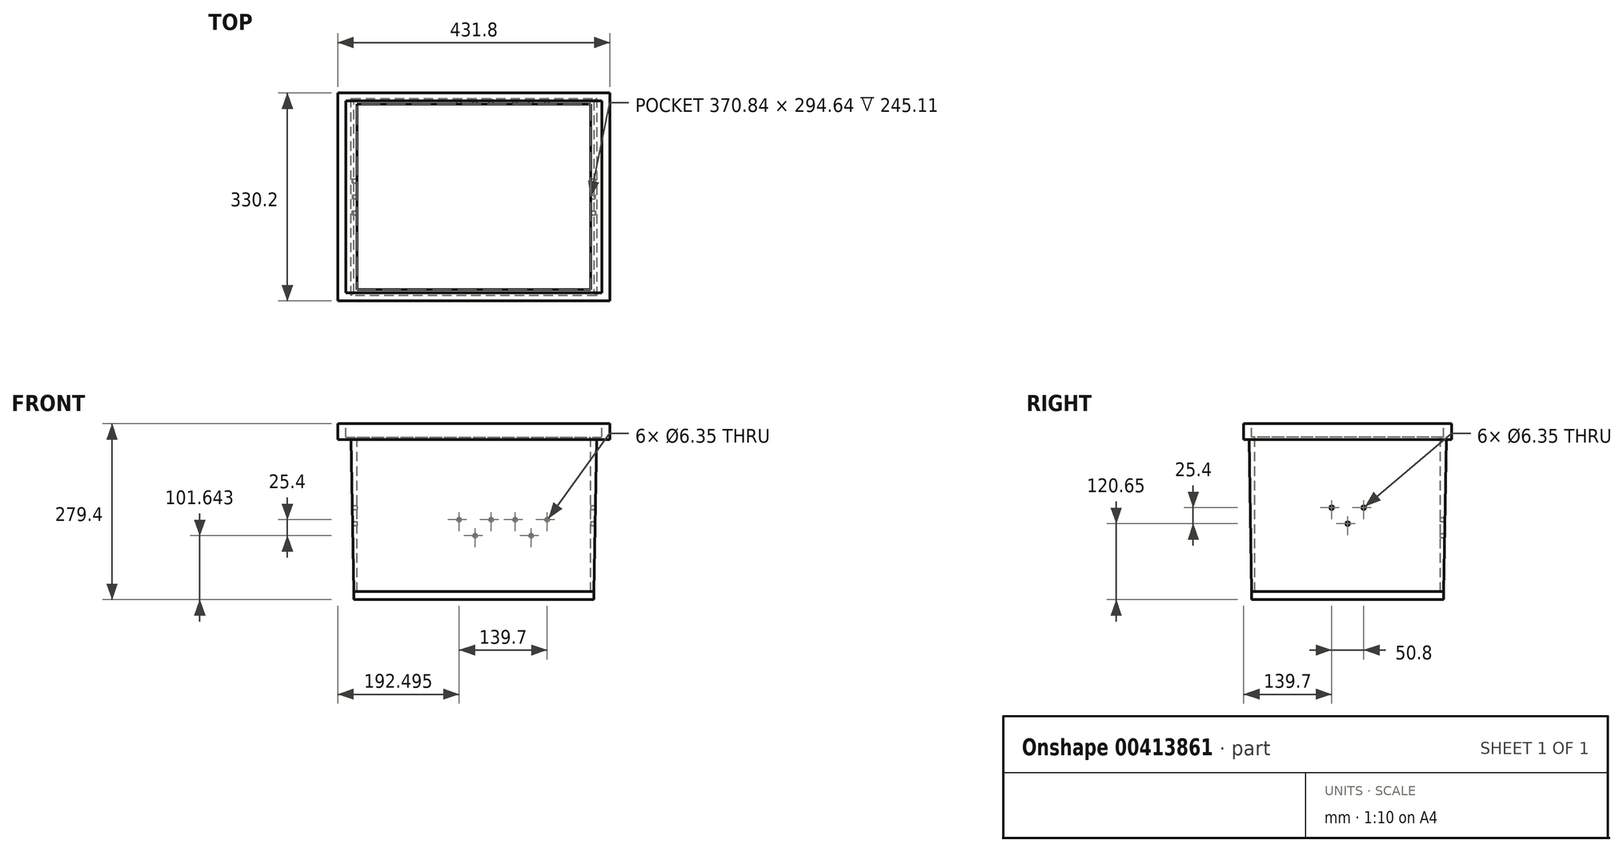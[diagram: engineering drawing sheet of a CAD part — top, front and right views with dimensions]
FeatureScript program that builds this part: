
annotation { "Feature Type Name" : "Feature", "Feature Type Description" : "" }
export const myFeature = defineFeature(function(context is Context, id is Id, definition is map)
    precondition{}
    {
        {
            var Q0;
            Q0=qCreatedBy(makeId("Top.planeOp"),FACE);
            var sketch = newSketch(context, id + "F0", { "sketchPlane" : qUnion([Q0])});
            skLineSegment(sketch, "E0.bottom", {"start": v(-190.5, 152.4) * mm, "end": v(190.5, 152.4) * mm});
            skLineSegment(sketch, "E0.top", {"start": v(-190.5, -152.4) * mm, "end": v(190.5, -152.4) * mm});
            skLineSegment(sketch, "E0.left", {"start": v(-190.5, 152.4) * mm, "end": v(-190.5, -152.4) * mm});
            skLineSegment(sketch, "E0.right", {"start": v(190.5, 152.4) * mm, "end": v(190.5, -152.4) * mm});
            skPoint(sketch, "E0.middle", {"position": v(0, 0) * mm});
            skLineSegment(sketch, "E1.0", {"start": v(-185.42, -147.32) * mm, "end": v(185.42, -147.32) * mm});
            skLineSegment(sketch, "E1.1", {"start": v(-185.42, 147.32) * mm, "end": v(-185.42, -147.32) * mm});
            skLineSegment(sketch, "E1.2", {"start": v(-185.42, 147.32) * mm, "end": v(185.42, 147.32) * mm});
            skLineSegment(sketch, "E1.3", {"start": v(185.42, 147.32) * mm, "end": v(185.42, -147.32) * mm});
            skSolve(sketch);
        }
        {
            var Q0;
            Q0 = qSketchRegion(id + "F0", true);
            extrude(context, id + "F1", {"entities" : qUnion([Q0]), "depth" : 241.3 * mm, "hasDraft" : true, "draftAngle" : 1 * degree});
        }
        {
            var Q0;
            Q0=makeQuery(id+"F1.opExtrude","CAP_FACE",FACE,{"disambiguationData":[OSD([sQuery(id+"F0.wireOp",EDGE,"E0.bottom"),sQuery(id+"F0.wireOp",EDGE,"E0.top"),sQuery(id+"F0.wireOp",EDGE,"E0.left"),sQuery(id+"F0.wireOp",EDGE,"E0.right"),sQuery(id+"F0.wireOp",EDGE,"E1.0"),sQuery(id+"F0.wireOp",EDGE,"E1.1"),sQuery(id+"F0.wireOp",EDGE,"E1.2"),sQuery(id+"F0.wireOp",EDGE,"E1.3")])],"isStart":false});
            var sketch = newSketch(context, id + "F2", { "sketchPlane" : qUnion([Q0])});
            skLineSegment(sketch, "E2.bottom", {"start": v(-215.9, 165.1) * mm, "end": v(215.9, 165.1) * mm});
            skLineSegment(sketch, "E2.top", {"start": v(-215.9, -165.1) * mm, "end": v(215.9, -165.1) * mm});
            skLineSegment(sketch, "E2.left", {"start": v(-215.9, 165.1) * mm, "end": v(-215.9, -165.1) * mm});
            skLineSegment(sketch, "E2.right", {"start": v(215.9, 165.1) * mm, "end": v(215.9, -165.1) * mm});
            skPoint(sketch, "E2.middle", {"position": v(0, 0) * mm});
            skSolve(sketch);
        }
        {
            var Q0;
            Q0 = qSketchRegion(id + "F2", true);
            extrude(context, id + "F3", {"entities" : qUnion([Q0]), "operationType" : NewBodyOperationType.ADD, "depth" : 25.4 * mm});
        }
        {
            var Q0;
            Q0=makeQuery(id+"F1.opExtrude","CAP_FACE",FACE,{"disambiguationData":[OSD([sQuery(id+"F0.wireOp",EDGE,"E0.bottom"),sQuery(id+"F0.wireOp",EDGE,"E0.top"),sQuery(id+"F0.wireOp",EDGE,"E0.left"),sQuery(id+"F0.wireOp",EDGE,"E0.right"),sQuery(id+"F0.wireOp",EDGE,"E1.0"),sQuery(id+"F0.wireOp",EDGE,"E1.1"),sQuery(id+"F0.wireOp",EDGE,"E1.2"),sQuery(id+"F0.wireOp",EDGE,"E1.3")])],"isStart":true});
            var sketch = newSketch(context, id + "F4", { "sketchPlane" : qUnion([Q0])});
            skLineSegment(sketch, "E3.0", {"start": v(-190.5, -152.4) * mm, "end": v(-190.5, 152.4) * mm});
            skLineSegment(sketch, "E3.1", {"start": v(-190.5, 152.4) * mm, "end": v(190.5, 152.4) * mm});
            skLineSegment(sketch, "E3.2", {"start": v(-190.5, -152.4) * mm, "end": v(190.5, -152.4) * mm});
            skLineSegment(sketch, "E3.3", {"start": v(190.5, -152.4) * mm, "end": v(190.5, 152.4) * mm});
            skSolve(sketch);
        }
        {
            var Q0;
            Q0 = qSketchRegion(id + "F4", true);
            extrude(context, id + "F5", {"entities" : qUnion([Q0]), "operationType" : NewBodyOperationType.ADD, "depth" : 12.7 * mm});
        }
        {
            var Q0;
            Q0=makeQuery(id+"F3.opExtrude","CAP_FACE",FACE,{"disambiguationData":[OSD([sQuery(id+"F2.wireOp",EDGE,"E2.bottom"),sQuery(id+"F2.wireOp",EDGE,"E2.top"),sQuery(id+"F2.wireOp",EDGE,"E2.left"),sQuery(id+"F2.wireOp",EDGE,"E2.right")])],"isStart":false});
            var sketch = newSketch(context, id + "F6", { "sketchPlane" : qUnion([Q0])});
            skLineSegment(sketch, "E4.0", {"start": v(-215.9, 165.1) * mm, "end": v(215.9, 165.1) * mm});
            skLineSegment(sketch, "E4.1", {"start": v(215.9, 165.1) * mm, "end": v(215.9, -165.1) * mm});
            skLineSegment(sketch, "E4.2", {"start": v(-215.9, -165.1) * mm, "end": v(215.9, -165.1) * mm});
            skLineSegment(sketch, "E4.3", {"start": v(-215.9, 165.1) * mm, "end": v(-215.9, -165.1) * mm});
            skLineSegment(sketch, "E5.0", {"start": v(-203.2, 152.4) * mm, "end": v(203.2, 152.4) * mm});
            skLineSegment(sketch, "E5.1", {"start": v(-203.2, 152.4) * mm, "end": v(-203.2, -152.4) * mm});
            skLineSegment(sketch, "E5.2", {"start": v(-203.2, -152.4) * mm, "end": v(203.2, -152.4) * mm});
            skLineSegment(sketch, "E5.3", {"start": v(203.2, 152.4) * mm, "end": v(203.2, -152.4) * mm});
            skSolve(sketch);
        }
        {
            var Q0;
            Q0=makeQuery(id+"F6.imprint","IMPRINT",FACE,{"disambiguationData":[TD([[makeQuery(id+"F6.imprint","IMPRINT",EDGE,{"derivedFrom":sQuery(id+"F6.wireOp",EDGE,"E5.0")}),-1.0]])]});
            extrude(context, id + "F7", {"entities" : qUnion([Q0]), "operationType" : NewBodyOperationType.REMOVE, "oppositeDirection" : true, "depth" : 21.59 * mm});
        }
        {
            var Q0;
            Q0=makeQuery(id+"F7.boolean.opBoolean","COPY",FACE,{"derivedFrom":makeQuery(id+"F7.opExtrude","CAP_FACE",FACE,{"disambiguationData":[OSD([sQuery(id+"F6.wireOp",EDGE,"E5.0"),sQuery(id+"F6.wireOp",EDGE,"E5.1"),sQuery(id+"F6.wireOp",EDGE,"E5.2"),sQuery(id+"F6.wireOp",EDGE,"E5.3")])],"isStart":false})});
            var sketch = newSketch(context, id + "F8", { "sketchPlane" : qUnion([Q0])});
            skLineSegment(sketch, "E6.0", {"start": v(-185.42, 147.32) * mm, "end": v(185.42, 147.32) * mm});
            skLineSegment(sketch, "E7.0", {"start": v(185.42, 147.32) * mm, "end": v(185.42, -147.32) * mm});
            skLineSegment(sketch, "E8.0", {"start": v(-185.42, -147.32) * mm, "end": v(185.42, -147.32) * mm});
            skLineSegment(sketch, "E9.0", {"start": v(-185.42, 147.32) * mm, "end": v(-185.42, -147.32) * mm});
            skSolve(sketch);
        }
        {
            var Q0;
            Q0 = qSketchRegion(id + "F8", true);
            extrude(context, id + "F9", {"entities" : qUnion([Q0]), "operationType" : NewBodyOperationType.REMOVE, "endBound" : BoundingType.UP_TO_NEXT, "oppositeDirection" : true, "depth" : 25.4 * mm});
        }
        {
            var Q0;
            Q0=makeQuery(id+"F1.opExtrude","SWEPT_FACE",FACE,{"disambiguationData":[OSD([sQuery(id+"F0.wireOp",EDGE,"E0.bottom")])]});
            var sketch = newSketch(context, id + "F10", { "sketchPlane" : qUnion([Q0])});
            skLineSegment(sketch, "E10", {"start": v(-192.5, 116.96) * mm, "end": v(192.5, 116.96) * mm, "construction": true});
            skLineSegment(sketch, "E11.0", {"start": v(190.5, -10.04) * mm, "end": v(-190.5, -10.04) * mm});
            skCircle(sketch, "E12", {"center": v(-116.3, 116.96) * mm, "radius": 3.18 * mm});
            skCircle(sketch, "E13", {"center": v(-65.5, 116.96) * mm, "radius": 3.18 * mm});
            skCircle(sketch, "E14", {"center": v(-27.4, 116.96) * mm, "radius": 3.18 * mm});
            skCircle(sketch, "E15", {"center": v(23.4, 116.96) * mm, "radius": 3.18 * mm});
            skCircle(sketch, "E16", {"center": v(-2, 91.56) * mm, "radius": 3.18 * mm});
            skCircle(sketch, "E17", {"center": v(-90.9, 91.56) * mm, "radius": 3.18 * mm});
            skLineSegment(sketch, "E18", {"start": v(-90.9, 91.56) * mm, "end": v(-90.9, 116.96) * mm, "construction": true});
            skSolve(sketch);
        }
        {
            var Q0;
            Q0 = qSketchRegion(id + "F10", true);
            extrude(context, id + "F11", {"entities" : qUnion([Q0]), "operationType" : NewBodyOperationType.REMOVE, "oppositeDirection" : true, "depth" : 76.2 * mm});
        }
        {
            var Q0;
            Q0=makeQuery(id+"F9.boolean.opBoolean","COPY",FACE,{"derivedFrom":makeQuery(id+"F9.opExtrude","SWEPT_FACE",FACE,{"disambiguationData":[OSD([sQuery(id+"F8.wireOp",EDGE,"E7.0")])]})});
            cPlane(context, id + "F12", {"entities" : qUnion([Q0]), "cplaneType" : CPlaneType.OFFSET, "offset" : 127 * mm, "oppositeDirection" : true, "width" : 152.4 * mm, "height" : 152.4 * mm});
        }
        {
            var Q0;
            Q0=qCreatedBy(id+"F12.planeOp",FACE);
            var sketch = newSketch(context, id + "F13", { "sketchPlane" : qUnion([Q0])});
            skCircle(sketch, "E19", {"center": v(-25.4, 133.35) * mm, "radius": 3.18 * mm});
            skCircle(sketch, "E20", {"center": v(25.4, 133.35) * mm, "radius": 3.18 * mm});
            skCircle(sketch, "E21", {"center": v(0, 107.95) * mm, "radius": 3.18 * mm});
            skLineSegment(sketch, "E22.0", {"start": v(156.61, 241.3) * mm, "end": v(152.4, 0) * mm});
            skPoint(sketch, "E23", {"position": v(154.5, 133.35) * mm});
            skLineSegment(sketch, "E24", {"start": v(154.5, 133.35) * mm, "end": v(-201.37, 133.35) * mm, "construction": true});
            skLineSegment(sketch, "E25", {"start": v(0, 133.35) * mm, "end": v(0, 107.95) * mm, "construction": true});
            skSolve(sketch);
        }
        {
            var Q0;
            Q0 = qSketchRegion(id + "F13", true);
            extrude(context, id + "F14", {"entities" : qUnion([Q0]), "operationType" : NewBodyOperationType.REMOVE, "endBound" : BoundingType.THROUGH_ALL, "depth" : 25.4 * mm});
        }
    });
